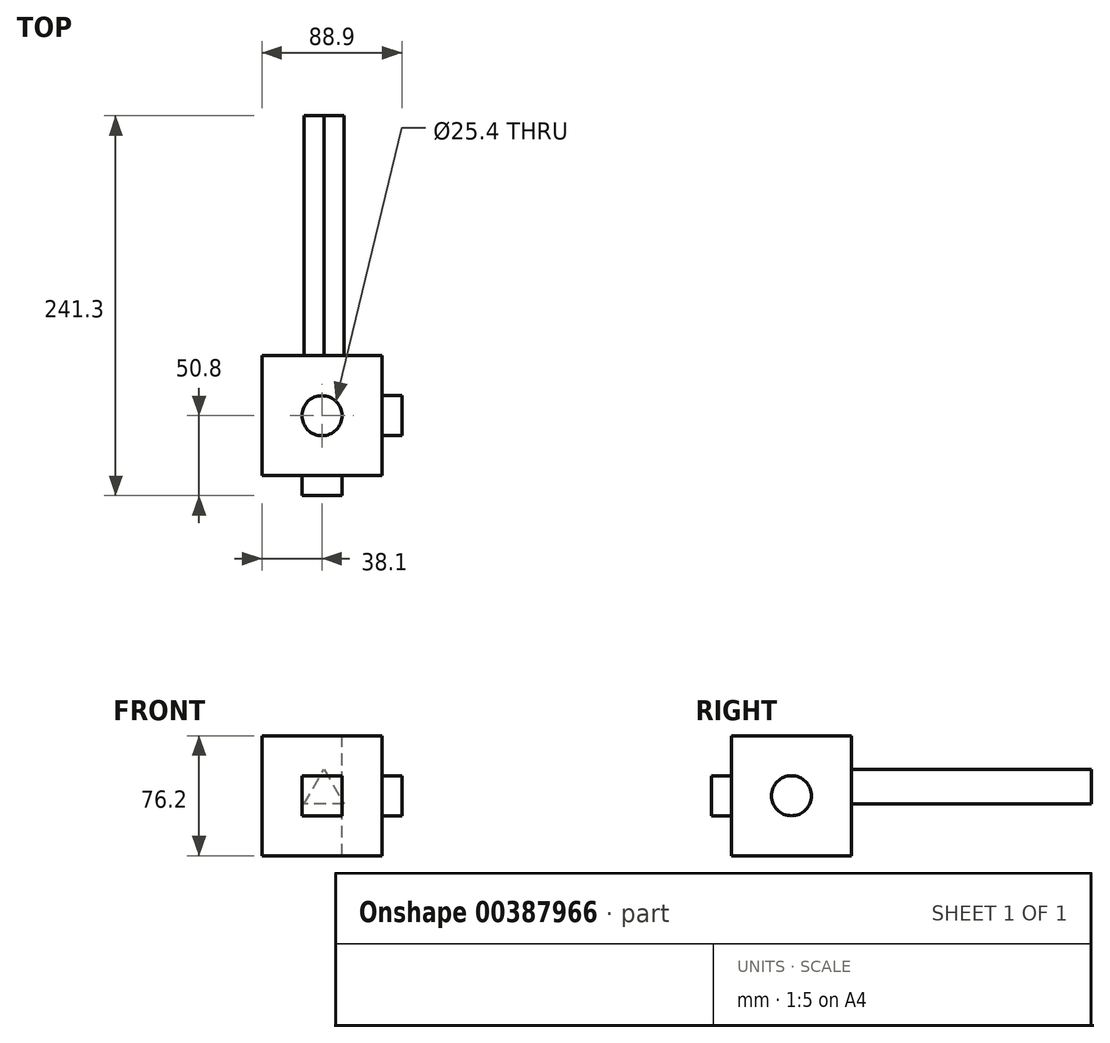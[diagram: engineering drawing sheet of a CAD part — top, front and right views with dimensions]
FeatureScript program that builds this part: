
annotation { "Feature Type Name" : "Feature", "Feature Type Description" : "" }
export const myFeature = defineFeature(function(context is Context, id is Id, definition is map)
    precondition{}
    {
        {
            var Q0;
            Q0=qCreatedBy(makeId("Front.planeOp"),FACE);
            var sketch = newSketch(context, id + "F0", { "sketchPlane" : qUnion([Q0])});
            skLineSegment(sketch, "E0.bottom", {"start": v(-37.73, 36.95) * mm, "end": v(38.47, 36.95) * mm});
            skLineSegment(sketch, "E0.top", {"start": v(-37.73, -39.25) * mm, "end": v(38.47, -39.25) * mm});
            skLineSegment(sketch, "E0.left", {"start": v(-37.73, 36.95) * mm, "end": v(-37.73, -39.25) * mm});
            skLineSegment(sketch, "E0.right", {"start": v(38.47, 36.95) * mm, "end": v(38.47, -39.25) * mm});
            skSolve(sketch);
        }
        {
            var Q0;
            Q0=makeQuery(id+"F0.imprint","IMPRINT",FACE,{"disambiguationData":[TD([[makeQuery(id+"F0.imprint","IMPRINT",EDGE,{"derivedFrom":sQuery(id+"F0.wireOp",EDGE,"E0.bottom")}),-1.0]])]});
            extrude(context, id + "F1", {"entities" : qUnion([Q0]), "depth" : 76.2 * mm});
        }
        {
            var Q0;
            Q0=makeQuery(id+"F1.opExtrude","SWEPT_FACE",FACE,{"disambiguationData":[OSD([sQuery(id+"F0.wireOp",EDGE,"E0.bottom")])]});
            var sketch = newSketch(context, id + "F2", { "sketchPlane" : qUnion([Q0])});
            skPoint(sketch, "E1", {"position": v(0.37, -38.1) * mm});
            skSolve(sketch);
        }
        {
            var Q0;
            Q0=sQuery(id+"F2.wireOp",VERTEX,"E1");
            var Q1;
            Q1=makeQuery(id+"F1.opExtrude","SWEPT_BODY",BODY,{"disambiguationData":[OSD([sQuery(id+"F0.wireOp",EDGE,"E0.bottom"),sQuery(id+"F0.wireOp",EDGE,"E0.top"),sQuery(id+"F0.wireOp",EDGE,"E0.left"),sQuery(id+"F0.wireOp",EDGE,"E0.right")])]});
            hole(context, id + "F3", {"style" : HoleStyle.SIMPLE, "endStyle" : HoleEndStyle.THROUGH, "holeDiameter" : 25.4 * mm, "isTappedThrough" : true, "tappedDepth" : 12.7 * mm, "tapClearance" : 3, "locations" : qUnion([Q0]), "scope" : qUnion([Q1])});
        }
        {
            var Q0;
            Q0=makeQuery(id+"F1.opExtrude","CAP_FACE",FACE,{"disambiguationData":[OSD([sQuery(id+"F0.wireOp",EDGE,"E0.bottom"),sQuery(id+"F0.wireOp",EDGE,"E0.top"),sQuery(id+"F0.wireOp",EDGE,"E0.left"),sQuery(id+"F0.wireOp",EDGE,"E0.right")])],"isStart":false});
            var sketch = newSketch(context, id + "F4", { "sketchPlane" : qUnion([Q0])});
            skLineSegment(sketch, "E2.bottom", {"start": v(-12.33, 11.55) * mm, "end": v(13.07, 11.55) * mm});
            skLineSegment(sketch, "E2.top", {"start": v(-12.33, -13.85) * mm, "end": v(13.07, -13.85) * mm});
            skLineSegment(sketch, "E2.left", {"start": v(-12.33, 11.55) * mm, "end": v(-12.33, -13.85) * mm});
            skLineSegment(sketch, "E2.right", {"start": v(13.07, 11.55) * mm, "end": v(13.07, -13.85) * mm});
            skSolve(sketch);
        }
        {
            var Q0;
            Q0=makeQuery(id+"F4.imprint","IMPRINT",FACE,{"disambiguationData":[TD([[makeQuery(id+"F4.imprint","IMPRINT",EDGE,{"derivedFrom":sQuery(id+"F4.wireOp",EDGE,"E2.bottom")}),-1.0]])]});
            extrude(context, id + "F5", {"entities" : qUnion([Q0]), "operationType" : NewBodyOperationType.ADD, "depth" : 12.7 * mm});
        }
        {
            var Q0;
            Q0=makeQuery(id+"F1.opExtrude","SWEPT_FACE",FACE,{"disambiguationData":[OSD([sQuery(id+"F0.wireOp",EDGE,"E0.right")])]});
            var sketch = newSketch(context, id + "F6", { "sketchPlane" : qUnion([Q0])});
            skCircle(sketch, "E3", {"center": v(-38.1, -1.15) * mm, "radius": 12.7 * mm});
            skSolve(sketch);
        }
        {
            var Q0;
            Q0 = qSketchRegion(id + "F6", true);
            extrude(context, id + "F7", {"entities" : qUnion([Q0]), "operationType" : NewBodyOperationType.ADD, "depth" : 12.7 * mm});
        }
        {
            var Q0;
            Q0=makeQuery(id+"F1.opExtrude","CAP_FACE",FACE,{"disambiguationData":[OSD([sQuery(id+"F0.wireOp",EDGE,"E0.bottom"),sQuery(id+"F0.wireOp",EDGE,"E0.top"),sQuery(id+"F0.wireOp",EDGE,"E0.left"),sQuery(id+"F0.wireOp",EDGE,"E0.right")])],"isStart":true});
            var sketch = newSketch(context, id + "F8", { "sketchPlane" : qUnion([Q0])});
            skLineSegment(sketch, "E4", {"start": v(-1.8, 15.6) * mm, "end": v(-14.5, -6.4) * mm});
            skLineSegment(sketch, "E5", {"start": v(-14.5, -6.4) * mm, "end": v(10.9, -6.4) * mm});
            skLineSegment(sketch, "E6", {"start": v(10.9, -6.4) * mm, "end": v(-1.8, 15.6) * mm});
            skSolve(sketch);
        }
        {
            var Q0;
            Q0 = qSketchRegion(id + "F8", true);
            extrude(context, id + "F9", {"entities" : qUnion([Q0]), "operationType" : NewBodyOperationType.ADD, "depth" : 152.4 * mm});
        }
    });
